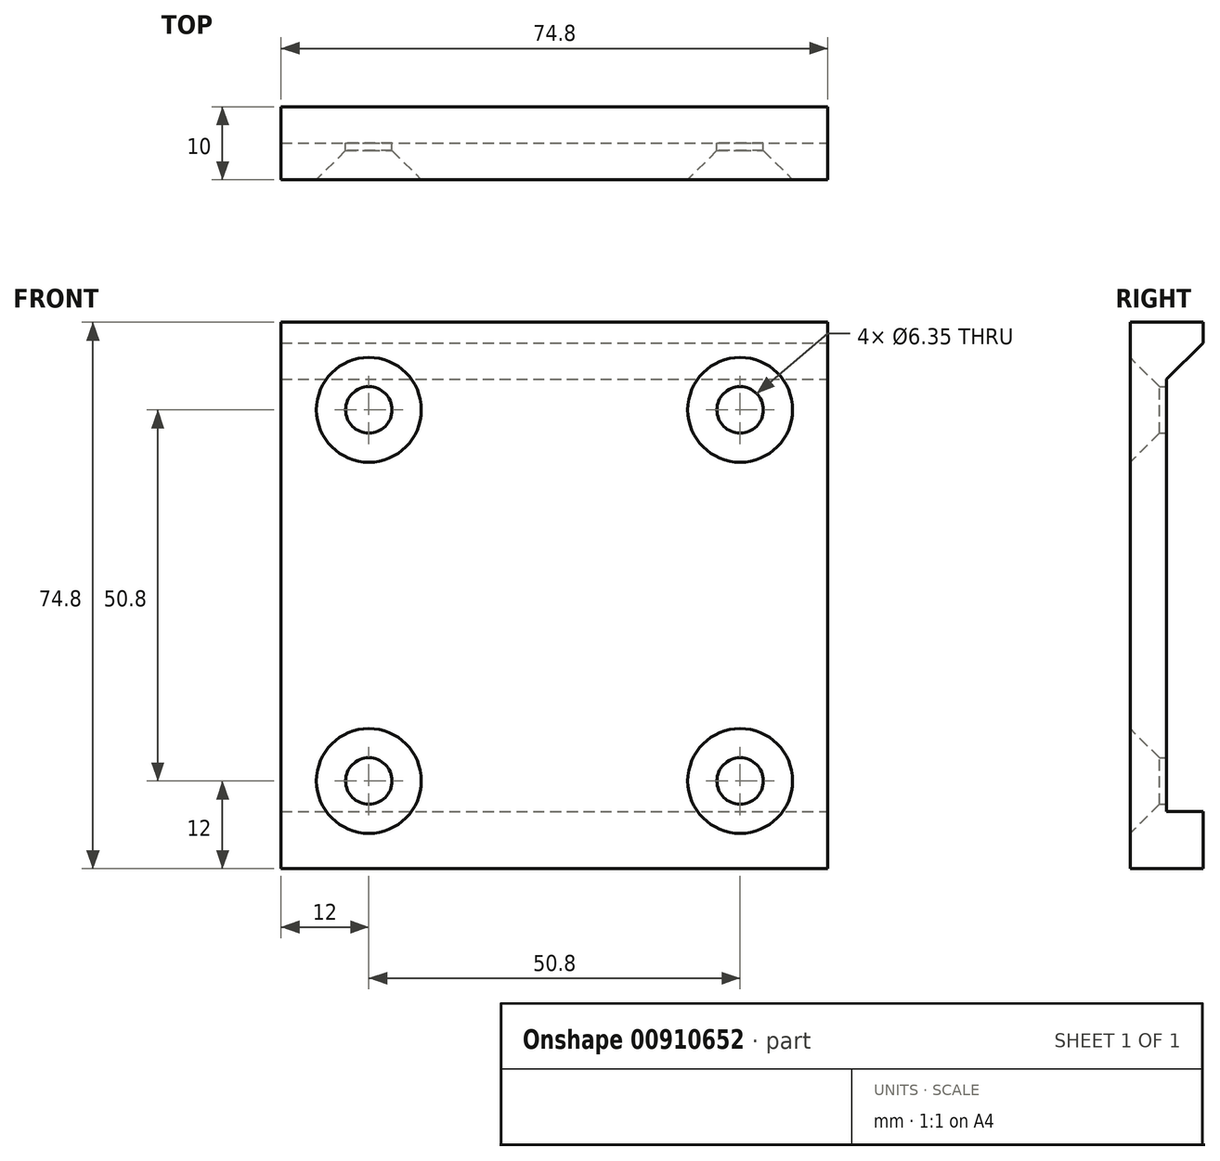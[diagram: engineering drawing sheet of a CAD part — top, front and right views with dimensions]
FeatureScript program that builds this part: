
annotation { "Feature Type Name" : "Feature", "Feature Type Description" : "" }
export const myFeature = defineFeature(function(context is Context, id is Id, definition is map)
    precondition{}
    {
        {
            var Q0;
            Q0=qCreatedBy(makeId("Front.planeOp"),FACE);
            var sketch = newSketch(context, id + "F0", { "sketchPlane" : qUnion([Q0])});
            skLineSegment(sketch, "E0.bottom", {"start": v(-74.8, 74.8) * mm, "end": v(0, 74.8) * mm});
            skLineSegment(sketch, "E0.top", {"start": v(-74.8, 0) * mm, "end": v(0, 0) * mm});
            skLineSegment(sketch, "E0.left", {"start": v(-74.8, 74.8) * mm, "end": v(-74.8, 0) * mm});
            skLineSegment(sketch, "E0.right", {"start": v(0, 74.8) * mm, "end": v(0, 0) * mm});
            skCircle(sketch, "E1", {"center": v(-62.8, 62.8) * mm, "radius": 3.18 * mm});
            skCircle(sketch, "E2", {"center": v(-12, 62.8) * mm, "radius": 3.18 * mm});
            skCircle(sketch, "E3", {"center": v(-62.8, 12) * mm, "radius": 3.18 * mm});
            skCircle(sketch, "E4", {"center": v(-12, 12) * mm, "radius": 3.18 * mm});
            skCircle(sketch, "E5", {"center": v(-12, 12) * mm, "radius": 12 * mm, "construction": true});
            skCircle(sketch, "E6", {"center": v(-62.8, 12) * mm, "radius": 12 * mm, "construction": true});
            skCircle(sketch, "E7", {"center": v(-62.8, 62.8) * mm, "radius": 12 * mm, "construction": true});
            skCircle(sketch, "E8", {"center": v(-12, 62.8) * mm, "radius": 12 * mm, "construction": true});
            skLineSegment(sketch, "E9.bottom", {"start": v(-62.8, 62.8) * mm, "end": v(-12, 62.8) * mm, "construction": true});
            skLineSegment(sketch, "E9.top", {"start": v(-62.8, 12) * mm, "end": v(-12, 12) * mm, "construction": true});
            skLineSegment(sketch, "E9.left", {"start": v(-62.8, 62.8) * mm, "end": v(-62.8, 12) * mm, "construction": true});
            skLineSegment(sketch, "E9.right", {"start": v(-12, 62.8) * mm, "end": v(-12, 12) * mm, "construction": true});
            skLineSegment(sketch, "E10.bottom", {"start": v(-65.98, 65.98) * mm, "end": v(-8.83, 65.98) * mm, "construction": true});
            skLineSegment(sketch, "E10.top", {"start": v(-65.98, 8.83) * mm, "end": v(-8.82, 8.83) * mm, "construction": true});
            skLineSegment(sketch, "E10.left", {"start": v(-65.98, 65.98) * mm, "end": v(-65.98, 8.83) * mm, "construction": true});
            skLineSegment(sketch, "E10.right", {"start": v(-8.83, 65.98) * mm, "end": v(-8.83, 8.83) * mm, "construction": true});
            skSolve(sketch);
        }
        {
            var Q0;
            Q0=makeQuery(id+"F0.imprint","IMPRINT",FACE,{"disambiguationData":[TD([[makeQuery(id+"F0.imprint","IMPRINT",EDGE,{"derivedFrom":sQuery(id+"F0.wireOp",EDGE,"E0.bottom")}),-1.0]])]});
            extrude(context, id + "F1", {"entities" : qUnion([Q0]), "depth" : 10 * mm, "offsetDistance" : 25 * mm});
        }
        {
            var Q0;
            Q0=makeQuery(id+"F1.opExtrude","SWEPT_FACE",FACE,{"disambiguationData":[OSD([sQuery(id+"F0.wireOp",EDGE,"E0.right")])]});
            var sketch = newSketch(context, id + "F2", { "sketchPlane" : qUnion([Q0])});
            skLineSegment(sketch, "E11.0", {"start": v(0, 59.63) * mm, "end": v(0, 65.98) * mm});
            skLineSegment(sketch, "E12.0", {"start": v(0, 8.83) * mm, "end": v(0, 15.18) * mm});
            skLineSegment(sketch, "E13", {"start": v(0, 71.98) * mm, "end": v(-5, 66.98) * mm});
            skLineSegment(sketch, "E14", {"start": v(-5, 66.98) * mm, "end": v(-5, 7.83) * mm});
            skLineSegment(sketch, "E15", {"start": v(-5, 7.83) * mm, "end": v(0, 7.83) * mm});
            skLineSegment(sketch, "E16", {"start": v(0, 7.83) * mm, "end": v(0, 71.98) * mm});
            skLineSegment(sketch, "E17", {"start": v(-5, 66.98) * mm, "end": v(0, 66.98) * mm, "construction": true});
            skLineSegment(sketch, "E18", {"start": v(0, 66.98) * mm, "end": v(0, 65.98) * mm, "construction": true});
            skSolve(sketch);
        }
        {
            var Q0;
            {var subQ0=sQuery(id+"F2.wireOp",EDGE,"E13");Q0=makeQuery(id+"F2.imprint","IMPRINT",FACE,{"disambiguationData":[TD([[makeQuery(id+"F2.imprint","IMPRINT",EDGE,{"derivedFrom":subQ0}),1.0]])]});}
            extrude(context, id + "F3", {"entities" : qUnion([Q0]), "operationType" : NewBodyOperationType.REMOVE, "endBound" : BoundingType.THROUGH_ALL, "oppositeDirection" : true, "depth" : 25 * mm, "offsetDistance" : 25 * mm});
        }
        {
            var Q0;
            Q0=makeQuery(id+"F1.opExtrude","CAP_EDGE",EDGE,{"disambiguationData":[OSD([sQuery(id+"F0.wireOp",EDGE,"E1")])],"isStart":false});
            var Q1;
            Q1=makeQuery(id+"F1.opExtrude","CAP_EDGE",EDGE,{"disambiguationData":[OSD([sQuery(id+"F0.wireOp",EDGE,"E2")])],"isStart":false});
            var Q2;
            Q2=makeQuery(id+"F1.opExtrude","CAP_EDGE",EDGE,{"disambiguationData":[OSD([sQuery(id+"F0.wireOp",EDGE,"E4")])],"isStart":false});
            var Q3;
            Q3=makeQuery(id+"F1.opExtrude","CAP_EDGE",EDGE,{"disambiguationData":[OSD([sQuery(id+"F0.wireOp",EDGE,"E3")])],"isStart":false});
            chamfer(context, id + "F4", {"entities" : qUnion([Q0, Q1, Q2, Q3]), "width" : 4 * mm, "tangentPropagation" : true});
        }
    });
